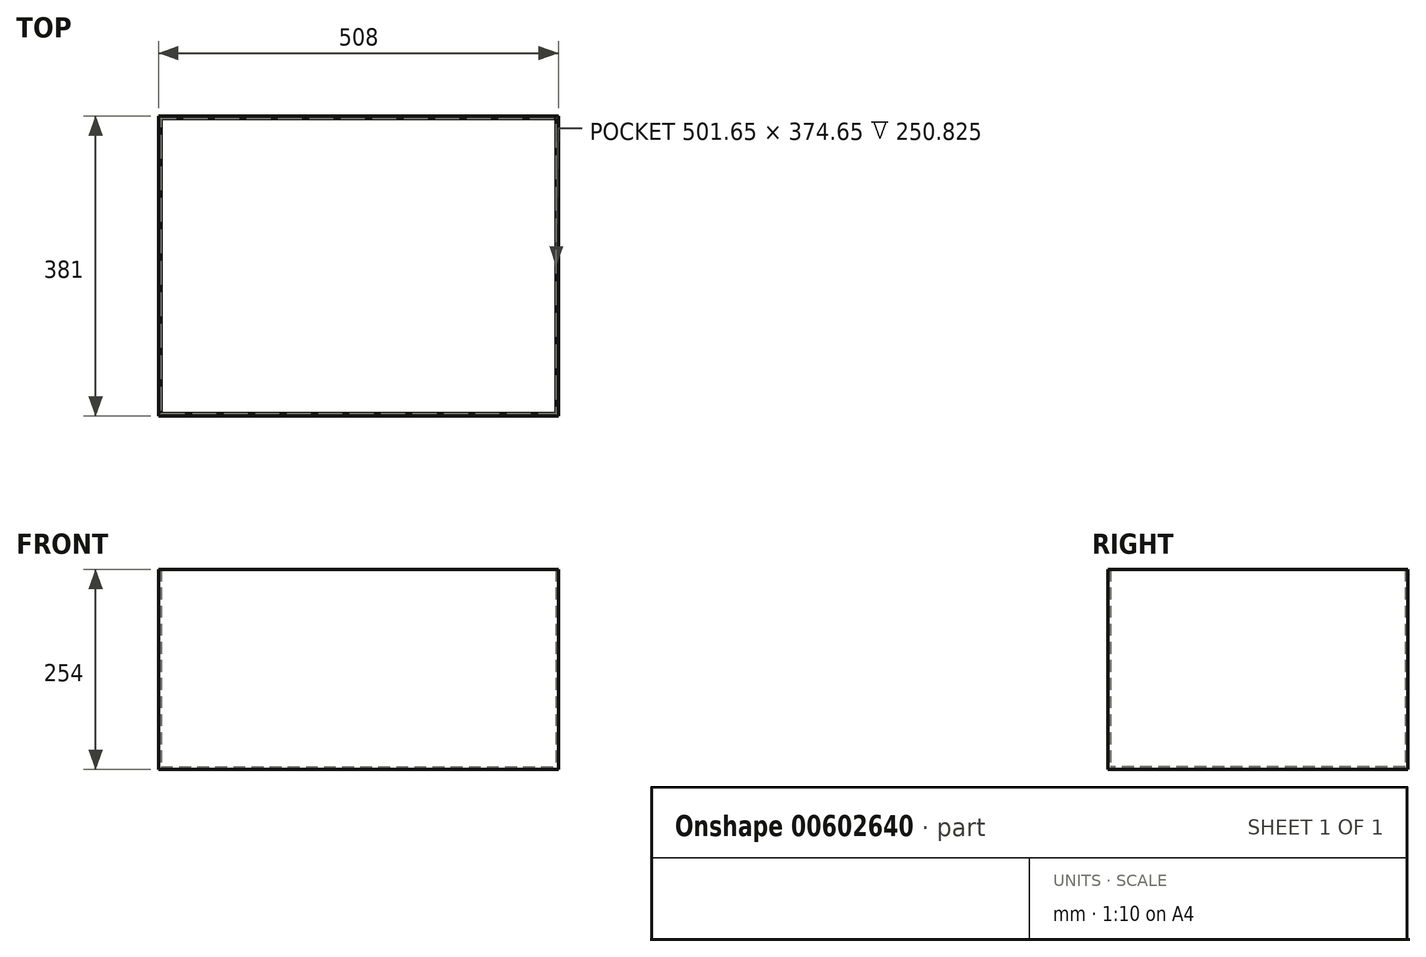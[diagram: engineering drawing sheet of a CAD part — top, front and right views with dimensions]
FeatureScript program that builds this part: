
annotation { "Feature Type Name" : "Feature", "Feature Type Description" : "" }
export const myFeature = defineFeature(function(context is Context, id is Id, definition is map)
    precondition{}
    {
        {
            var Q0;
            Q0=qCreatedBy(makeId("Top.planeOp"),FACE);
            var sketch = newSketch(context, id + "F0", { "sketchPlane" : qUnion([Q0])});
            skLineSegment(sketch, "E0", {"start": v(-254, 190.5) * mm, "end": v(254, -190.5) * mm, "construction": true});
            skLineSegment(sketch, "E1.bottom", {"start": v(-254, 190.5) * mm, "end": v(254, 190.5) * mm});
            skLineSegment(sketch, "E1.top", {"start": v(-254, -190.5) * mm, "end": v(254, -190.5) * mm});
            skLineSegment(sketch, "E1.left", {"start": v(-254, 190.5) * mm, "end": v(-254, -190.5) * mm});
            skLineSegment(sketch, "E1.right", {"start": v(254, 190.5) * mm, "end": v(254, -190.5) * mm});
            skSolve(sketch);
        }
        {
            var Q0;
            Q0=makeQuery(id+"F0.imprint","IMPRINT",FACE,{"disambiguationData":[TD([[makeQuery(id+"F0.imprint","IMPRINT",EDGE,{"derivedFrom":sQuery(id+"F0.wireOp",EDGE,"E1.bottom")}),-1.0]])]});
            extrude(context, id + "F1", {"entities" : qUnion([Q0]), "depth" : 254 * mm, "offsetDistance" : 25.4 * mm});
        }
        {
            var Q0;
            Q0=makeQuery(id+"F1.opExtrude","CAP_FACE",FACE,{"disambiguationData":[OSD([sQuery(id+"F0.wireOp",EDGE,"E1.bottom"),sQuery(id+"F0.wireOp",EDGE,"E1.top"),sQuery(id+"F0.wireOp",EDGE,"E1.left"),sQuery(id+"F0.wireOp",EDGE,"E1.right")])],"isStart":false});
            shell(context, id + "F2", {"entities" : qUnion([Q0]), "thickness" : 3.17 * mm});
        }
    });
